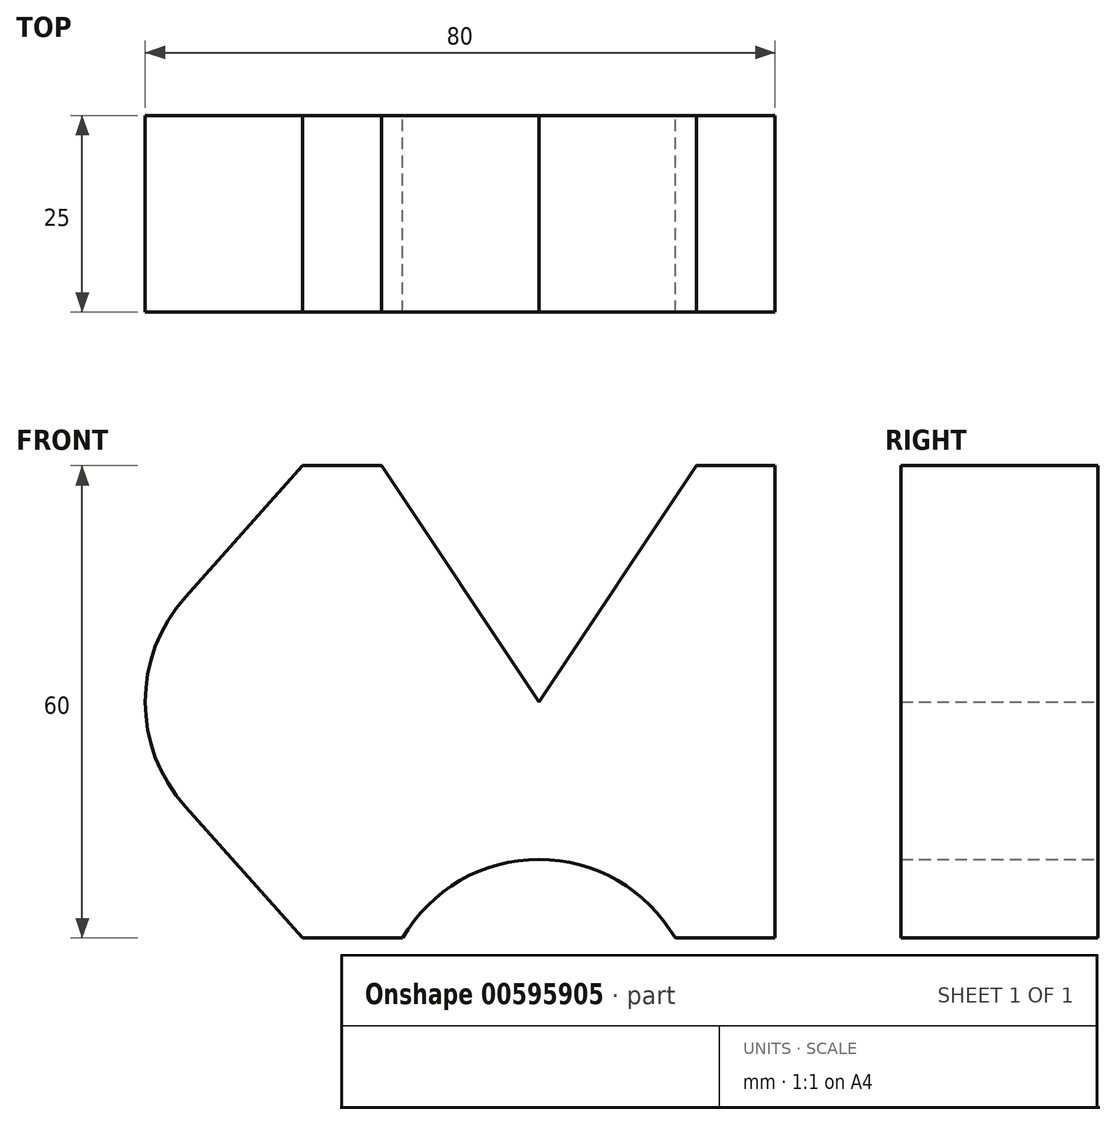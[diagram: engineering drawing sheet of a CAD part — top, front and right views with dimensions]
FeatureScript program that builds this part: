
annotation { "Feature Type Name" : "Feature", "Feature Type Description" : "" }
export const myFeature = defineFeature(function(context is Context, id is Id, definition is map)
    precondition{}
    {
        {
            var Q0;
            Q0=qCreatedBy(makeId("Front.planeOp"),FACE);
            var sketch = newSketch(context, id + "F0", { "sketchPlane" : qUnion([Q0])});
            skLineSegment(sketch, "E0", {"start": v(0, 0) * mm, "end": v(20, 30) * mm});
            skLineSegment(sketch, "E1", {"start": v(20, 30) * mm, "end": v(30, 30) * mm});
            skLineSegment(sketch, "E2", {"start": v(30, 30) * mm, "end": v(30, -30) * mm});
            skLineSegment(sketch, "E3", {"start": v(30, -30) * mm, "end": v(17.32, -30) * mm});
            skLineSegment(sketch, "E4", {"start": v(0, 0) * mm, "end": v(-20, 30) * mm});
            skLineSegment(sketch, "E5", {"start": v(-20, 30) * mm, "end": v(-30, 30) * mm});
            skLineSegment(sketch, "E6", {"start": v(-30, 30) * mm, "end": v(-44.9, 13.33) * mm});
            skArc(sketch, "E7", {"start": v(-44.9, 13.33) * mm, "mid": v(-50, 0) * mm, "end": v(-44.9, -13.33) * mm});
            skArc(sketch, "E8", {"start": v(17.32, -30) * mm, "mid": v(0, -20) * mm, "end": v(-17.32, -30) * mm});
            skLineSegment(sketch, "E9", {"start": v(-17.32, -30) * mm, "end": v(-30, -30) * mm});
            skLineSegment(sketch, "E10", {"start": v(-30, -30) * mm, "end": v(-44.9, -13.33) * mm});
            skSolve(sketch);
        }
        {
            var Q0;
            Q0 = qSketchRegion(id + "F0", true);
            extrude(context, id + "F1", {"entities" : qUnion([Q0]), "depth" : 25 * mm, "offsetDistance" : 25 * mm});
        }
    });
